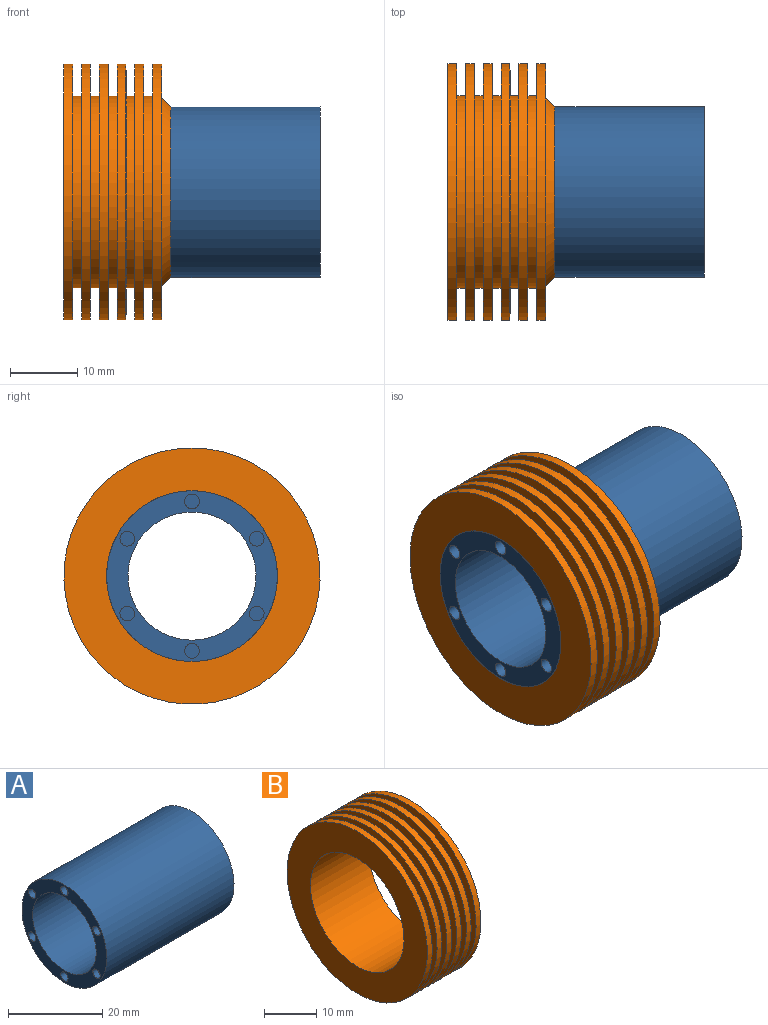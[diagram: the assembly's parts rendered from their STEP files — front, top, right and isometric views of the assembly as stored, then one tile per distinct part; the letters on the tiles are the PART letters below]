
ASSEMBLY  parts=2 mates=1
PART A: 16 faces, bbox 38.1x25.4x25.4 mm
  f0: plane 25.4x25.4mm, normal (1,0,0), area 221.7mm2, adj f1,f3
  f1: cylinder r=12.7mm len=38.1mm, axis (1,0,0), area 3040.2mm2, adj f0,f2
  f2: plane 25.4x25.4mm, normal (-1,0,0), area 199.2mm2, adj f1,f3,f4,f6,f8,f10,f12,f14
  f3: cylinder r=9.53mm len=38.1mm, axis (1,0,0), area 2280.2mm2, adj f0,f2
  f4: cylinder r=1.09mm len=6.35mm, axis (-1,0,0), area 43.6mm2, adj f2,f5
  f5: plane 2.18x2.18mm, normal (-1,0,0), area 3.7mm2, adj f4
  f6: cylinder r=1.09mm len=6.35mm, axis (-1,0,0), area 43.6mm2, adj f2,f7
  f7: plane 2.18x2.18mm, normal (-1,0,0), area 3.7mm2, adj f6
  f8: cylinder r=1.09mm len=6.35mm, axis (-1,0,0), area 43.6mm2, adj f2,f9
  f9: plane 2.18x2.18mm, normal (-1,0,0), area 3.7mm2, adj f8
  f10: cylinder r=1.09mm len=6.35mm, axis (-1,0,0), area 43.6mm2, adj f2,f11
  f11: plane 2.18x2.18mm, normal (-1,0,0), area 3.7mm2, adj f10
  f12: cylinder r=1.09mm len=6.35mm, axis (-1,0,0), area 43.6mm2, adj f2,f13
  f13: plane 2.18x2.18mm, normal (-1,0,0), area 3.7mm2, adj f12
  f14: cylinder r=1.09mm len=6.35mm, axis (-1,0,0), area 43.6mm2, adj f2,f15
  f15: plane 2.18x2.18mm, normal (-1,0,0), area 3.7mm2, adj f14
PART B: 25 faces, bbox 15.9x38.1x38.1 mm
  f0: cylinder r=19.05mm len=38.1mm, axis (-1,0,0), area 157.1mm2, adj f1,f24
  f1: plane 38.1x38.1mm, normal (-1,0,0), area 498.8mm2, adj f0,f2
  f2: cylinder r=14.29mm len=28.58mm, axis (-1,0,0), area 117.8mm2, adj f1,f3
  f3: cone r=19.05mm half-angle=89.7deg, axis (-1,0,0), area 498.8mm2, adj f2,f4
  f4: cylinder r=19.05mm len=38.1mm, axis (-1,0,0), area 157.1mm2, adj f3,f5
  f5: plane 38.1x38.1mm, normal (-1,0,0), area 498.8mm2, adj f4,f6
  f6: cylinder r=14.29mm len=28.58mm, axis (-1,0,0), area 119.7mm2, adj f5,f7
  f7: plane 38.1x38.1mm, normal (1,0,0), area 498.8mm2, adj f6,f8
  f8: cylinder r=19.05mm len=38.1mm, axis (-1,0,0), area 157.1mm2, adj f7,f9
  f9: plane 38.1x38.1mm, normal (-1,0,0), area 498.8mm2, adj f8,f10
  f10: cylinder r=14.29mm len=28.58mm, axis (-1,0,0), area 117.8mm2, adj f9,f11
  f11: plane 38.1x38.1mm, normal (1,0,0), area 498.8mm2, adj f10,f12
  f12: cylinder r=19.05mm len=38.1mm, axis (-1,0,0), area 157.1mm2, adj f11,f13
  f13: plane 38.1x38.1mm, normal (-1,0,0), area 633.4mm2, adj f12,f14
  f14: cylinder r=12.7mm len=25.4mm, axis (-1,0,0), area 1266.9mm2, adj f13,f15
  f15: cone r=12.7mm half-angle=44.1deg, axis (-1,0,0), area 158.3mm2, adj f14,f16
  f16: plane 38.1x38.1mm, normal (1,0,0), area 523.2mm2, adj f15,f17
  f17: cylinder r=19.05mm len=38.1mm, axis (-1,0,0), area 157.1mm2, adj f16,f18
  f18: plane 38.1x38.1mm, normal (-1,0,0), area 498.8mm2, adj f17,f19
  f19: cylinder r=14.29mm len=28.58mm, axis (-1,0,0), area 117.8mm2, adj f18,f20
  f20: cone r=19.05mm half-angle=89.7deg, axis (-1,0,0), area 498.8mm2, adj f19,f21
  f21: cylinder r=19.05mm len=38.1mm, axis (-1,0,0), area 157.1mm2, adj f20,f22
  f22: plane 38.1x38.1mm, normal (-1,0,0), area 498.8mm2, adj f21,f23
  f23: cylinder r=14.29mm len=28.58mm, axis (-1,0,0), area 117.8mm2, adj f22,f24
  f24: cone r=19.05mm half-angle=89.7deg, axis (-1,0,0), area 498.8mm2, adj f0,f23
PLACE A t=(92.22,30.71,4.06)mm
PLACE B t=(54.12,30.71,4.06)mm
MATE planar A.f1 <-> B.f0  axis (-1,0,0) through (54.12,30.71,4.06)mm
